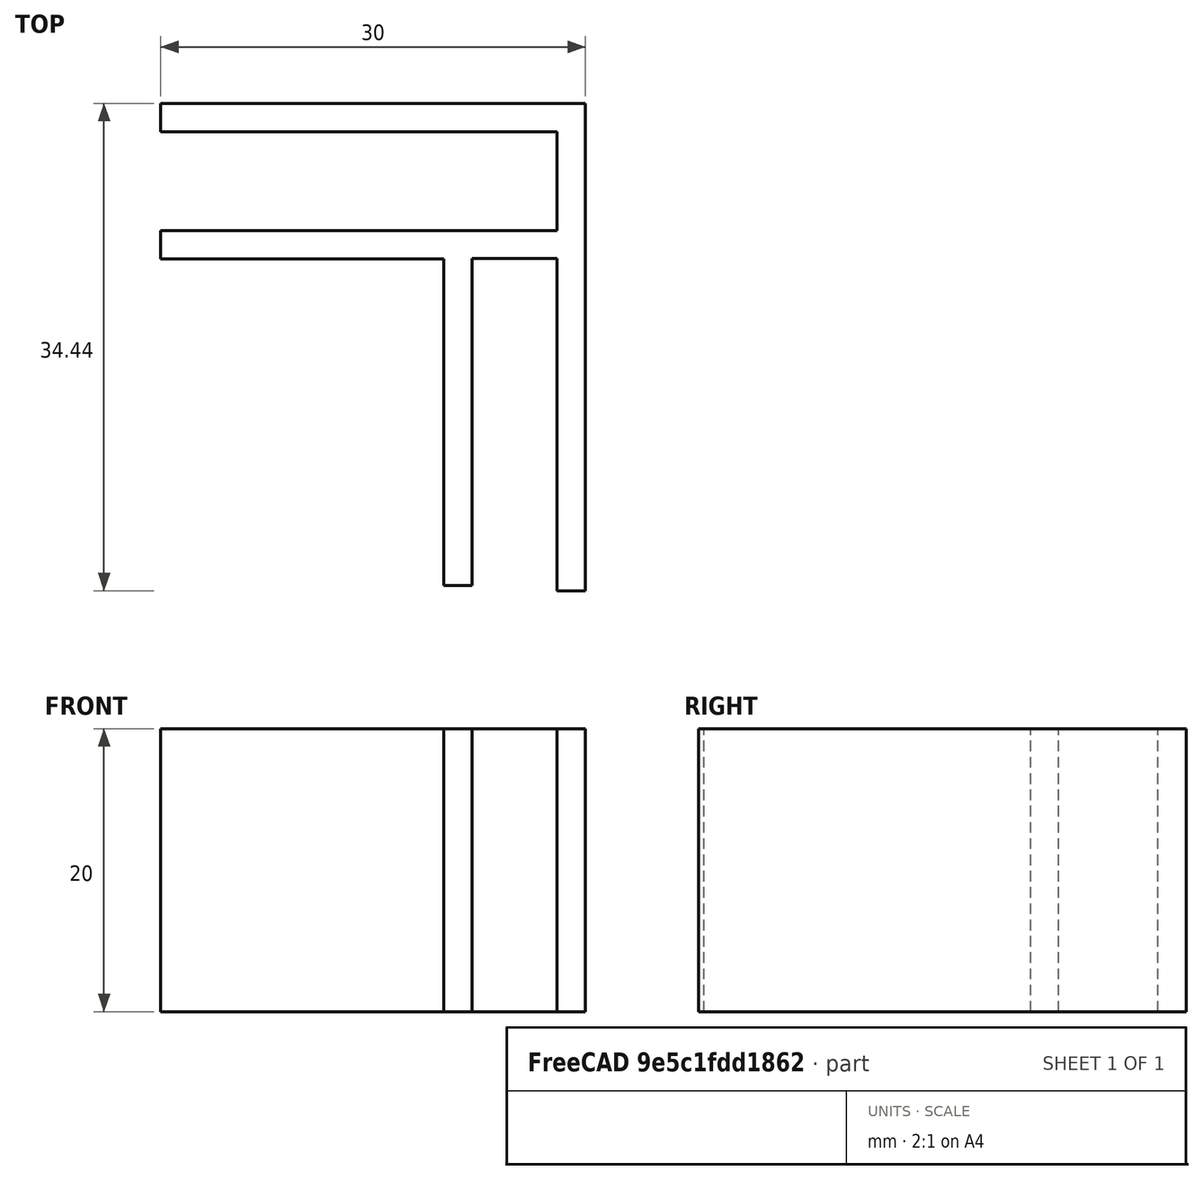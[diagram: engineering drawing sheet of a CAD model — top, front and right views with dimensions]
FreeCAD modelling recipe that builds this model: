
FCSTD DOCUMENT  (FreeCAD 0.19R24366 (Git))
Label: lid-holder
License: All rights reserved
LicenseURL: http://en.wikipedia.org/wiki/All_rights_reserved
objects: Sketcher::SketchObject×1, PartDesign::Pad×1, PartDesign::Body×1
note: 4 computed .brp shape members not serialized (recipe doc carries the construction recipe); baked Part::Feature solids carry a one-line shape summary decoded from their .brp

FEATURE [Sketcher::SketchObject] Sketch
  FullyConstrained = false
  MapMode = 5
  Support = -> [XY_Plane]
  sketch-geometry (14):
    g0: LineSegment StartX=0 StartY=45.948 StartZ=0 EndX=0 EndY=22.873 EndZ=0
    g1: LineSegment StartX=0 StartY=22.873 StartZ=0 EndX=2 EndY=22.873 EndZ=0
    g2: LineSegment StartX=2 StartY=22.873 StartZ=0 EndX=2 EndY=45.9781 EndZ=0
    g3: LineSegment StartX=2 StartY=45.9781 StartZ=0 EndX=8 EndY=45.9781 EndZ=0
    g4: LineSegment StartX=8 StartY=45.9781 StartZ=0 EndX=8 EndY=22.5062 EndZ=0
    g5: LineSegment StartX=8 StartY=22.5062 StartZ=0 EndX=10 EndY=22.5062 EndZ=0
    g6: LineSegment StartX=10 StartY=22.5062 StartZ=0 EndX=10 EndY=56.948 EndZ=0
    g7: LineSegment StartX=10 StartY=56.948 StartZ=0 EndX=-20 EndY=56.948 EndZ=0
    g8: LineSegment StartX=-20 StartY=56.948 StartZ=0 EndX=-20 EndY=54.948 EndZ=0
    g9: LineSegment StartX=-20 StartY=54.948 StartZ=0 EndX=8 EndY=54.948 EndZ=0
    g10: LineSegment StartX=8 StartY=54.948 StartZ=0 EndX=8 EndY=47.948 EndZ=0
    g11: LineSegment StartX=8 StartY=47.948 StartZ=0 EndX=-20 EndY=47.948 EndZ=0
    g12: LineSegment StartX=-20 StartY=47.948 StartZ=0 EndX=-20 EndY=45.948 EndZ=0
    g13: LineSegment StartX=-20 StartY=45.948 StartZ=0 EndX=0 EndY=45.948 EndZ=0
  constraints (38):
    c: PointOnObject(g0,g-2)
    c: PointOnObject(g0,g-2)
    c: Coincident(g0,g1)
    c: Horizontal(g1)
    c: Coincident(g1,g2)
    c: Vertical(g2)
    c: Coincident(g2,g3)
    c: Horizontal(g3)
    c: Coincident(g3,g4)
    c: Vertical(g4)
    c: Coincident(g4,g5)
    c: Horizontal(g5)
    c: Coincident(g5,g6)
    c: Vertical(g6)
    c: Coincident(g6,g7)
    c: Horizontal(g7)
    c: Coincident(g7,g8)
    c: Vertical(g8)
    c: Coincident(g8,g9)
    c: Horizontal(g9)
    c: Coincident(g9,g10)
    c: Vertical(g10)
    c: Coincident(g10,g11)
    c: Horizontal(g11)
    c: Coincident(g11,g12)
    c: Vertical(g12)
    c: Coincident(g12,g13)
    c: Coincident(g13,g0)
    c: Horizontal(g13)
    c: DistanceX(g1,g1) = 2
    c: DistanceX(g5,g5) = 2
    c: DistanceX(g3,g3) = 6
    c: DistanceY(g8,g8) = 2
    c: DistanceY(g12,g12) = 2
    c: DistanceY(g10,g10) = 7
    c: DistanceX(g7,g7) = 30
    c: DistanceX(g11,g6) = 30
    c: DistanceX(g11,g11) = 28
FEATURE [PartDesign::Pad] Pad
  Direction = (1,1,1)
  Length = 20
  Length2 = 100
  Profile = -> Sketch
  Type = 0
FEATURE [PartDesign::Body] Body
  Group = -> [Sketch,Pad]
  Origin = -> Origin
  Tip = -> Pad
